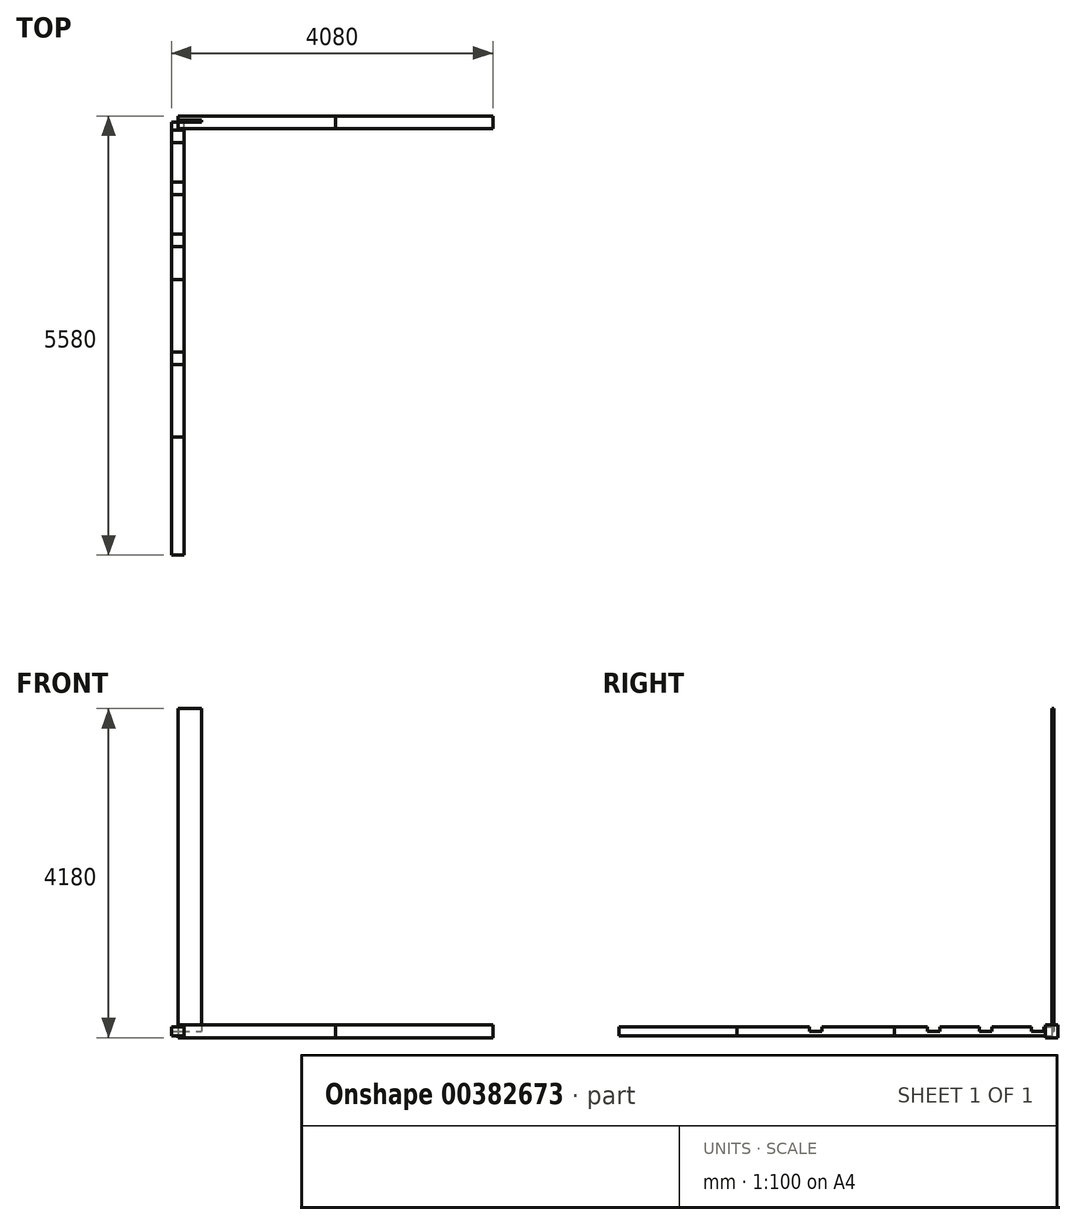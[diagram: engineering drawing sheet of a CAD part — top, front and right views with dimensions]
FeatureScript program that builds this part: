
annotation { "Feature Type Name" : "Feature", "Feature Type Description" : "" }
export const myFeature = defineFeature(function(context is Context, id is Id, definition is map)
    precondition{}
    {
        {
            var Q0;
            Q0=qCreatedBy(makeId("Front.planeOp"),FACE);
            var sketch = newSketch(context, id + "F0", { "sketchPlane" : qUnion([Q0])});
            skLineSegment(sketch, "E0.bottom", {"start": v(80, 60) * mm, "end": v(-80, 60) * mm});
            skLineSegment(sketch, "E0.top", {"start": v(80, -60) * mm, "end": v(-80, -60) * mm});
            skLineSegment(sketch, "E0.left", {"start": v(80, 60) * mm, "end": v(80, -60) * mm});
            skLineSegment(sketch, "E0.right", {"start": v(-80, 60) * mm, "end": v(-80, -60) * mm});
            skPoint(sketch, "E0.middle", {"position": v(0, 0) * mm});
            skSolve(sketch);
        }
        {
            var Q0;
            Q0 = qSketchRegion(id + "F0", true);
            extrude(context, id + "F1", {"entities" : qUnion([Q0]), "depth" : 2000 * mm});
        }
        {
            var Q0;
            Q0=makeQuery(id+"F1.opExtrude","CAP_FACE",FACE,{"disambiguationData":[OSD([sQuery(id+"F0.wireOp",EDGE,"E0.bottom"),sQuery(id+"F0.wireOp",EDGE,"E0.top"),sQuery(id+"F0.wireOp",EDGE,"E0.left"),sQuery(id+"F0.wireOp",EDGE,"E0.right")])],"isStart":false});
            extrude(context, id + "F2", {"entities" : qUnion([Q0]), "depth" : 2000 * mm});
        }
        {
            var Q0;
            Q0=makeQuery(id+"F1.opExtrude","SWEPT_FACE",FACE,{"disambiguationData":[OSD([sQuery(id+"F0.wireOp",EDGE,"E0.left")])]});
            var sketch = newSketch(context, id + "F3", { "sketchPlane" : qUnion([Q0])});
            skLineSegment(sketch, "E1.bottom", {"start": v(-100, 60) * mm, "end": v(-260, 60) * mm});
            skLineSegment(sketch, "E1.top", {"start": v(-100, 0) * mm, "end": v(-260, 0) * mm});
            skLineSegment(sketch, "E1.left", {"start": v(-100, 60) * mm, "end": v(-100, 0) * mm});
            skLineSegment(sketch, "E1.right", {"start": v(-260, 60) * mm, "end": v(-260, 0) * mm});
            skLineSegment(sketch, "E2.bottom", {"start": v(-760, 60) * mm, "end": v(-920, 60) * mm});
            skLineSegment(sketch, "E2.top", {"start": v(-760, 0) * mm, "end": v(-920, 0) * mm});
            skLineSegment(sketch, "E2.left", {"start": v(-760, 60) * mm, "end": v(-760, 0) * mm});
            skLineSegment(sketch, "E2.right", {"start": v(-920, 60) * mm, "end": v(-920, 0) * mm});
            skLineSegment(sketch, "E3.bottom", {"start": v(-1420, 60) * mm, "end": v(-1580, 60) * mm});
            skLineSegment(sketch, "E3.top", {"start": v(-1420, 0) * mm, "end": v(-1580, 0) * mm});
            skLineSegment(sketch, "E3.left", {"start": v(-1420, 60) * mm, "end": v(-1420, 0) * mm});
            skLineSegment(sketch, "E3.right", {"start": v(-1580, 60) * mm, "end": v(-1580, 0) * mm});
            skLineSegment(sketch, "E4.bottom", {"start": v(-2920, 60) * mm, "end": v(-3080, 60) * mm});
            skLineSegment(sketch, "E4.top", {"start": v(-2920, 0) * mm, "end": v(-3080, 0) * mm});
            skLineSegment(sketch, "E4.left", {"start": v(-2920, 60) * mm, "end": v(-2920, 0) * mm});
            skLineSegment(sketch, "E4.right", {"start": v(-3080, 60) * mm, "end": v(-3080, 0) * mm});
            skPoint(sketch, "E5", {"position": v(-3000, 0) * mm});
            skSolve(sketch);
        }
        {
            var Q0;
            Q0 = qSketchRegion(id + "F3", true);
            extrude(context, id + "F4", {"entities" : qUnion([Q0]), "operationType" : NewBodyOperationType.REMOVE, "endBound" : BoundingType.THROUGH_ALL, "oppositeDirection" : true, "depth" : 25 * mm});
        }
        {
            var Q0;
            Q0=qCreatedBy(makeId("Top.planeOp"),FACE);
            var sketch = newSketch(context, id + "F5", { "sketchPlane" : qUnion([Q0])});
            skLineSegment(sketch, "E6.bottom", {"start": v(0, 0) * mm, "end": v(300, 0) * mm});
            skLineSegment(sketch, "E6.top", {"start": v(0, 25) * mm, "end": v(300, 25) * mm});
            skLineSegment(sketch, "E6.left", {"start": v(0, 0) * mm, "end": v(0, 25) * mm});
            skLineSegment(sketch, "E6.right", {"start": v(300, 0) * mm, "end": v(300, 25) * mm});
            skSolve(sketch);
        }
        {
            var Q0;
            Q0 = qSketchRegion(id + "F5", true);
            extrude(context, id + "F6", {"entities" : qUnion([Q0]), "depth" : 4100 * mm});
        }
        {
            var Q0;
            Q0=qCreatedBy(makeId("Right.planeOp"),FACE);
            var sketch = newSketch(context, id + "F7", { "sketchPlane" : qUnion([Q0])});
            skLineSegment(sketch, "E7.bottom", {"start": v(-80, 80) * mm, "end": v(80, 80) * mm});
            skLineSegment(sketch, "E7.top", {"start": v(-80, -80) * mm, "end": v(80, -80) * mm});
            skLineSegment(sketch, "E7.left", {"start": v(-80, 80) * mm, "end": v(-80, -80) * mm});
            skLineSegment(sketch, "E7.right", {"start": v(80, 80) * mm, "end": v(80, -80) * mm});
            skPoint(sketch, "E7.middle", {"position": v(0, 0) * mm});
            skSolve(sketch);
        }
        {
            var Q0;
            Q0 = qSketchRegion(id + "F7", true);
            extrude(context, id + "F8", {"entities" : qUnion([Q0]), "depth" : 2000 * mm});
        }
        {
            var Q0;
            Q0=makeQuery(id+"F8.opExtrude","CAP_FACE",FACE,{"disambiguationData":[OSD([sQuery(id+"F7.wireOp",EDGE,"E7.bottom"),sQuery(id+"F7.wireOp",EDGE,"E7.top"),sQuery(id+"F7.wireOp",EDGE,"E7.left"),sQuery(id+"F7.wireOp",EDGE,"E7.right")])],"isStart":false});
            extrude(context, id + "F9", {"entities" : qUnion([Q0]), "depth" : 2000 * mm});
        }
        {
            var Q0;
            Q0=makeQuery(id+"F2.opExtrude","CAP_FACE",FACE,{"disambiguationData":[OSD([sQuery(id+"F0.wireOp",EDGE,"E0.bottom"),sQuery(id+"F0.wireOp",EDGE,"E0.top"),sQuery(id+"F0.wireOp",EDGE,"E0.left"),sQuery(id+"F0.wireOp",EDGE,"E0.right")])],"isStart":false});
            extrude(context, id + "F10", {"entities" : qUnion([Q0]), "depth" : 1500 * mm});
        }
    });
